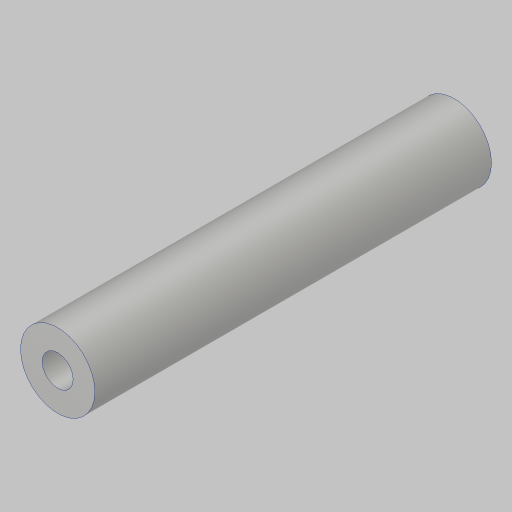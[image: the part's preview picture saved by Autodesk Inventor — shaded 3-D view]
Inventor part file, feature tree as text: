
AUTODESK INVENTOR PART (.ipt)
format: ipt  version: 2023.5 (Build 275446000, 446)  size: 105,472 bytes
history: native  units: in
note: dims shown in document units (in); Inventor stores cm internally (conversion verified against a paired STEP export)
features: extrude x1, hole x1
ambient origin geometry x8: Origin, YZ Plane, XZ Plane, XY Plane, X Axis, Y Axis, Z Axis, Center Point
bodies: Solid1 (feature_tree)
feature tree (2):
  extrude  "Extrusion1"  Depth=2.0in
  hole  "Hole1"  [1 undecoded]
note: 1 required parameter value undecoded (feature->parameter linkage not recoverable at this tier; creation-order binding heuristic only, values carry confidence <= 0.55)
